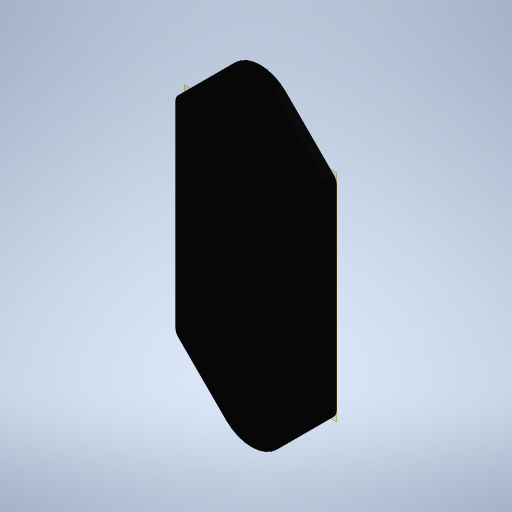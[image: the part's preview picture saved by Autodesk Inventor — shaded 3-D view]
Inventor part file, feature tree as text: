
AUTODESK INVENTOR PART (.ipt)
format: ipt  version: 2023 (Build 270158000, 158)  size: 253,440 bytes
history: native  units: mm
features: reference x6, fillet x2, sketch x2, other x2, plane x1, extrude x1, hole x1
ambient origin geometry x8: Origin, YZ Plane, XZ Plane, XY Plane, X Axis, Y Axis, Z Axis, Center Point
bodies: Solid1 (feature_tree)
feature tree (15):
  plane  "Work Plane1"
  extrude  "Extrusion1"  Depth=5.0mm
  fillet  "Fillet1"  Radius=5.0mm
  fillet  "Fillet2"  Radius=5.0mm
  hole  "Hole1"  [1 undecoded]
  sketch  "Sketch1"  dims[d0=45.0deg d1=35.0mm d2=5.0mm d3=0.0mm d4=5.0mm]
  reference  "Reference1"
  reference  "Reference2"
  reference  "Reference3"
  reference  "Reference4"
  reference  "Reference5"
  reference  "Reference6"
  sketch  "Sketch2"  dims[d5=20.0mm d6=6.0mm d7=6.0mm d8=6.5mm d9=6.0mm d10=4.0mm d11=2.0mm d12=90.0deg d13=8.0mm d14=20.594885mm]
  other  "<userpath>\Downloads\frame\parts\emergancy_stop\G_IC03_XX_12648V.iam"
  other  "G_IC03_XX_12648V.iam"
note: 1 required parameter value undecoded (feature->parameter linkage not recoverable at this tier; creation-order binding heuristic only, values carry confidence <= 0.55)
